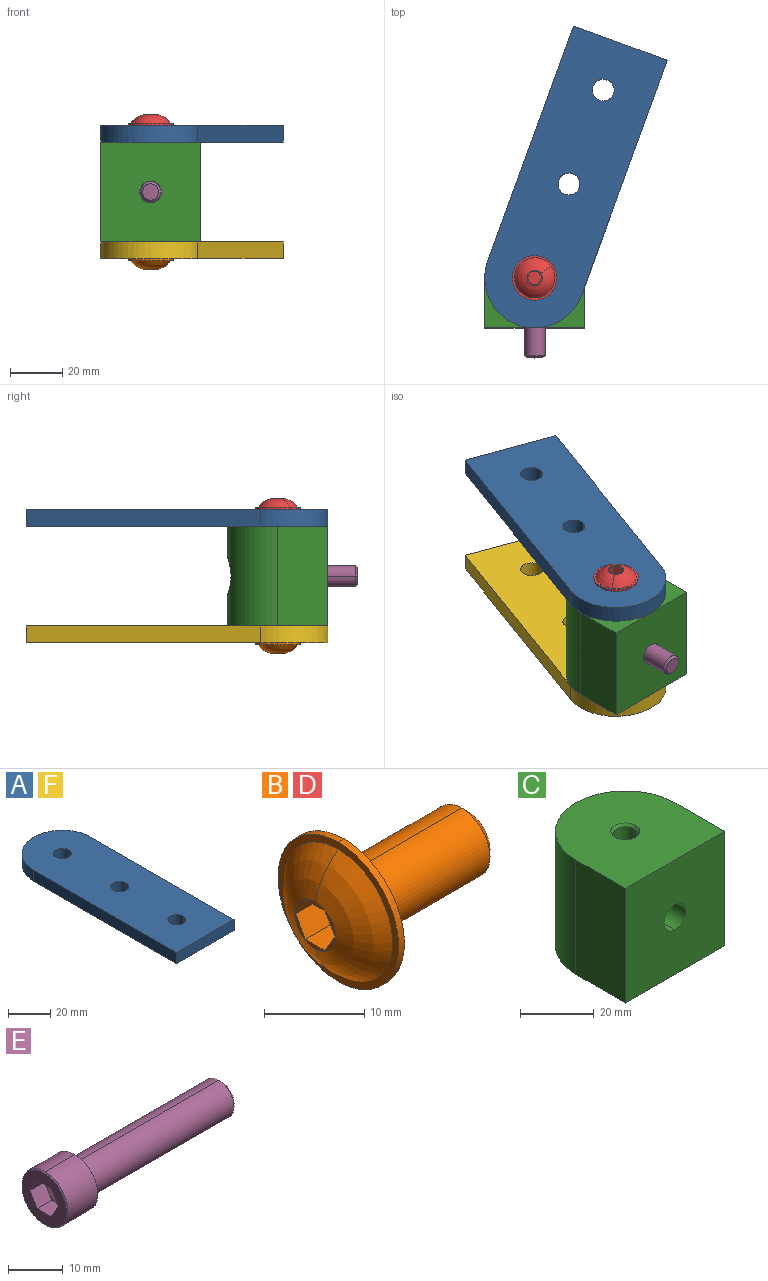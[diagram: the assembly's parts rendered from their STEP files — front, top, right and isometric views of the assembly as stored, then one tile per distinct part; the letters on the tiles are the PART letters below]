
ASSEMBLY  parts=6 mates=12
PART A: 12 faces, bbox 38.1x114.3x6.4 mm
  f0: cylinder r=19.05mm len=38.1mm, axis (0,0,1), area 380mm2, adj f1,f3,f4,f7
  f1: plane 95.25x6.35mm, normal (1,0,0), area 604.8mm2, adj f0,f2,f4,f7
  f2: plane 38.1x6.35mm, normal (0,-1,0), area 241.9mm2, adj f1,f3,f4,f7
  f3: plane 95.25x6.35mm, normal (-1,0,0), area 604.8mm2, adj f0,f2,f4,f7
  f4: plane 114.3x38.1mm, normal (0,0,1), area 4035.5mm2, adj f0,f1,f2,f3,f5,f6,f8,f9
  f5: cylinder r=4.17mm len=8.33mm, axis (0,0,1), area 83.1mm2, adj f4,f6,f7
  f6: cylinder r=4.17mm len=8.33mm, axis (0,0,1), area 83.1mm2, adj f4,f5,f7
  f7: plane 114.3x38.1mm, normal (0,0,-1), area 4035.5mm2, adj f0,f1,f2,f3,f5,f6,f8,f9
  f8: cylinder r=4.17mm len=8.33mm, axis (0,0,1), area 83.1mm2, adj f4,f7,f9
  f9: cylinder r=4.17mm len=8.33mm, axis (0,0,1), area 83.1mm2, adj f4,f7,f8
  f10: cylinder r=4.17mm len=8.33mm, axis (0,0,1), area 83.1mm2, adj f4,f7,f11
  f11: cylinder r=4.17mm len=8.33mm, axis (0,0,1), area 83.1mm2, adj f4,f7,f10
PART B: 19 faces, bbox 21.5x17x17 mm
  f0: torus R=0.76mm, axis (1,0,0), area 101mm2, adj f1,f2,f10
  f1: torus R=0.76mm, axis (1,0,0), area 101mm2, adj f0,f2,f10
  f2: plane 5.79x5.79mm, normal (-1,0,0), area 6.2mm2, adj f0,f1,f3,f4,f5,f6,f7,f8
  f3: plane 3.56x2.41mm, normal (0,-0.87,-0.5), area 9.9mm2, adj f2,f4,f8,f9
  f4: plane 3.56x2.79mm, normal (0,0,-1), area 9.9mm2, adj f2,f3,f5,f9
  f5: plane 3.56x2.41mm, normal (0,0.87,-0.5), area 9.9mm2, adj f2,f4,f6,f9
  f6: plane 3.56x2.41mm, normal (0,0.87,0.5), area 9.9mm2, adj f2,f5,f7,f9
  f7: plane 3.56x2.79mm, normal (0,0,1), area 9.9mm2, adj f2,f6,f8,f9
  f8: plane 3.56x2.41mm, normal (0,-0.87,0.5), area 9.9mm2, adj f2,f3,f7,f9
  f9: plane 5.57x4.83mm, normal (-1,0,0), area 20.2mm2, adj f3,f4,f5,f6,f7,f8
  f10: plane 17.02x17.02mm, normal (-1,0,0), area 43.2mm2, adj f0,f1,f11,f12
  f11: cylinder r=8.51mm len=17.02mm, axis (-1,0,0), area 21.7mm2, adj f10,f12,f13
  f12: cylinder r=8.51mm len=17.02mm, axis (-1,0,0), area 21.7mm2, adj f10,f11,f13
  f13: plane 17.02x17.02mm, normal (1,0,0), area 178mm2, adj f11,f12,f14,f15
  f14: cylinder r=3.97mm len=16.62mm, axis (-1,0,0), area 207.3mm2, adj f13,f15,f17
  f15: cylinder r=3.97mm len=16.62mm, axis (-1,0,0), area 207.3mm2, adj f13,f14,f16
  f16: cone r=3.97mm half-angle=45deg, axis (-1,0,0), area 13.2mm2, adj f15,f17,f18
  f17: cone r=3.97mm half-angle=45deg, axis (-1,0,0), area 13.2mm2, adj f14,f16,f18
  f18: plane 6.26x6.26mm, normal (1,0,0), area 30.8mm2, adj f16,f17
PART C: 19 faces, bbox 38.1x38.1x38.1 mm
  f0: plane 38.1x19.05mm, normal (-1,0,0), area 725.8mm2, adj f7,f9,f10,f14
  f1: cylinder r=4.17mm len=26.67mm, axis (0,1,0), area 313.6mm2, adj f2,f3,f4,f9,f13,f17,f18
  f2: cylinder r=4.17mm len=26.67mm, axis (0,1,0), area 313.6mm2, adj f1,f3,f4,f9,f13,f17,f18
  f3: cylinder r=3.21mm len=15.63mm, axis (0,0,1), area 149.8mm2, adj f1,f2,f4,f6
  f4: cylinder r=3.21mm len=15.63mm, axis (0,0,1), area 149.8mm2, adj f1,f2,f3,f5
  f5: cone r=3.21mm half-angle=45deg, axis (0,0,-1), area 12.2mm2, adj f4,f6,f7
  f6: cone r=3.21mm half-angle=45deg, axis (0,0,-1), area 12.2mm2, adj f3,f5,f7
  f7: plane 38.1x38.1mm, normal (0,0,-1), area 1246.4mm2, adj f0,f5,f6,f8,f9,f10
  f8: plane 38.1x19.05mm, normal (1,0,0), area 725.8mm2, adj f7,f9,f10,f14
  f9: plane 38.1x38.1mm, normal (0,-1,0), area 1397.1mm2, adj f0,f1,f2,f7,f8,f14
  f10: cylinder r=19.05mm len=38.1mm, axis (0,0,1), area 2143.7mm2, adj f0,f7,f8,f11,f12,f14
  f11: cylinder r=6.54mm len=13.08mm, axis (0,1,0), area 223.1mm2, adj f10,f12,f13
  f12: cylinder r=6.54mm len=13.08mm, axis (0,1,0), area 223.1mm2, adj f10,f11,f13
  f13: plane 13.08x13.08mm, normal (0,1,0), area 79.9mm2, adj f1,f2,f11,f12
  f14: plane 38.1x38.1mm, normal (0,0,1), area 1246.4mm2, adj f0,f8,f9,f10,f15,f16
  f15: cone r=3.97mm half-angle=45deg, axis (0,0,1), area 12.2mm2, adj f14,f16,f18
  f16: cone r=3.97mm half-angle=45deg, axis (0,0,1), area 12.2mm2, adj f14,f15,f17
  f17: cylinder r=3.21mm len=15.63mm, axis (0,0,1), area 149.8mm2, adj f1,f2,f16,f18
  f18: cylinder r=3.21mm len=15.63mm, axis (0,0,1), area 149.8mm2, adj f1,f2,f15,f17
PART D: same geometry as B
PART E: 27 faces, bbox 46x11.9x11.9 mm
  f0: cone r=3.17mm half-angle=60deg, axis (-1,0,0), area 18.3mm2, adj f1,f9,f10,f24
  f1: cone r=3.17mm half-angle=60deg, axis (-1,0,0), area 18.3mm2, adj f0,f2,f25,f26
  f2: plane 2.75x1.59mm, normal (-1,0,0), area 0.5mm2, adj f1,f3,f4
  f3: plane 3.84x3.67mm, normal (0,0,1), area 14.1mm2, adj f2,f4,f8,f9,f11
  f4: plane 3.84x3.18mm, normal (0,-0.87,0.5), area 14.1mm2, adj f2,f3,f5,f11,f26
  f5: plane 3.84x3.18mm, normal (0,-0.87,-0.5), area 14.1mm2, adj f4,f6,f11,f25,f26
  f6: plane 3.84x3.67mm, normal (0,0,-1), area 14.1mm2, adj f5,f7,f11,f24,f25
  f7: plane 3.84x3.18mm, normal (0,0.87,-0.5), area 14.1mm2, adj f6,f8,f10,f11,f24
  f8: plane 3.84x3.18mm, normal (0,0.87,0.5), area 14.1mm2, adj f3,f7,f9,f10,f11
  f9: plane 2.75x1.59mm, normal (-1,0,0), area 0.5mm2, adj f0,f3,f8
  f10: plane 3.18x0.92mm, normal (-1,0,0), area 0.5mm2, adj f0,f7,f8
  f11: plane 11.44x11.44mm, normal (-1,0,0), area 67.8mm2, adj f3,f4,f5,f6,f7,f8,f12,f13
  f12: cone r=5.72mm half-angle=45deg, axis (1,0,0), area 6.2mm2, adj f11,f13,f15
  f13: cone r=5.72mm half-angle=45deg, axis (1,0,0), area 6.2mm2, adj f11,f12,f14
  f14: cylinder r=5.96mm len=11.91mm, axis (-1,0,0), area 143.8mm2, adj f13,f15,f16
  f15: cylinder r=5.96mm len=11.91mm, axis (-1,0,0), area 143.8mm2, adj f12,f14,f16
  f16: plane 11.91x11.91mm, normal (1,0,0), area 55.9mm2, adj f14,f15,f17,f18
  f17: torus R=4.21mm, axis (1,0,0), area 4.8mm2, adj f16,f18,f20
  f18: torus R=4.21mm, axis (1,0,0), area 4.8mm2, adj f16,f17,f19
  f19: cylinder r=3.97mm len=37.02mm, axis (-1,0,0), area 461.6mm2, adj f18,f20,f22
  f20: cylinder r=3.97mm len=37.02mm, axis (-1,0,0), area 461.6mm2, adj f17,f19,f21
  f21: cone r=3.97mm half-angle=45deg, axis (-1,0,0), area 13.2mm2, adj f20,f22,f23
  f22: cone r=3.97mm half-angle=45deg, axis (-1,0,0), area 13.2mm2, adj f19,f21,f23
  f23: plane 6.26x6.26mm, normal (1,0,0), area 30.8mm2, adj f21,f22
  f24: plane 2.75x1.59mm, normal (-1,0,0), area 0.5mm2, adj f0,f6,f7
  f25: plane 2.75x1.59mm, normal (-1,0,0), area 0.5mm2, adj f1,f5,f6
  f26: plane 3.18x0.92mm, normal (-1,0,0), area 0.5mm2, adj f1,f4,f5
PART F: same geometry as A
PLACE A rot(axis=(0,0,1),160deg) t=(32.64,108.53,19.05)mm
PLACE B rot(axis=(0.71,0,0.71),180deg) t=(0,19.05,-25.4)mm
PLACE C at identity fixed
PLACE D rot(axis=(-0.28,0.92,0.28),95deg) t=(0,19.05,25.4)mm
PLACE E rot(axis=(0.58,-0.58,-0.58),120deg) t=(0,26.67,0)mm
PLACE F rot(axis=(0,0,1),160deg) t=(32.64,108.53,-25.4)mm
MATE planar A.f2 <-> F.f2  axis (0.34,0.94,0) through (32.64,108.53,22.22)mm
MATE planar C.f7 <-> F.f4  axis (0,0,-1) through (19.05,9.52,-19.05)mm
MATE cylindrical D.f11 <-> A.f0  axis (0,0,1) through (0,19.05,25.4)mm
MATE planar A.f1 <-> F.f1  axis (-0.94,0.34,0) through (-1.58,70.32,22.22)mm
MATE parallel E.f6 <-> C.f8  axis (1,0,0) through (-3.18,32.68,0)mm
MATE planar B.f0 <-> F.f7  axis (0,0,1) through (0,19.05,-25.4)mm
MATE cylindrical F.f0 <-> C.f3  axis (0,0,1) through (0,19.05,-25.4)mm
MATE cylindrical E.f0 <-> C.f1  axis (0,1,0) through (0,7.92,0)mm
MATE planar D.f13 <-> A.f4  axis (0,0,-1) through (-3.28,16.82,25.4)mm
MATE cylindrical B.f11 <-> F.f0  axis (0,0,-1) through (0,19.05,-25.4)mm
MATE planar A.f7 <-> C.f14  axis (0,0,-1) through (13.76,56.76,19.05)mm
MATE planar E.f0 <-> C.f1  axis (0,-1,0) through (0,26.67,0)mm
